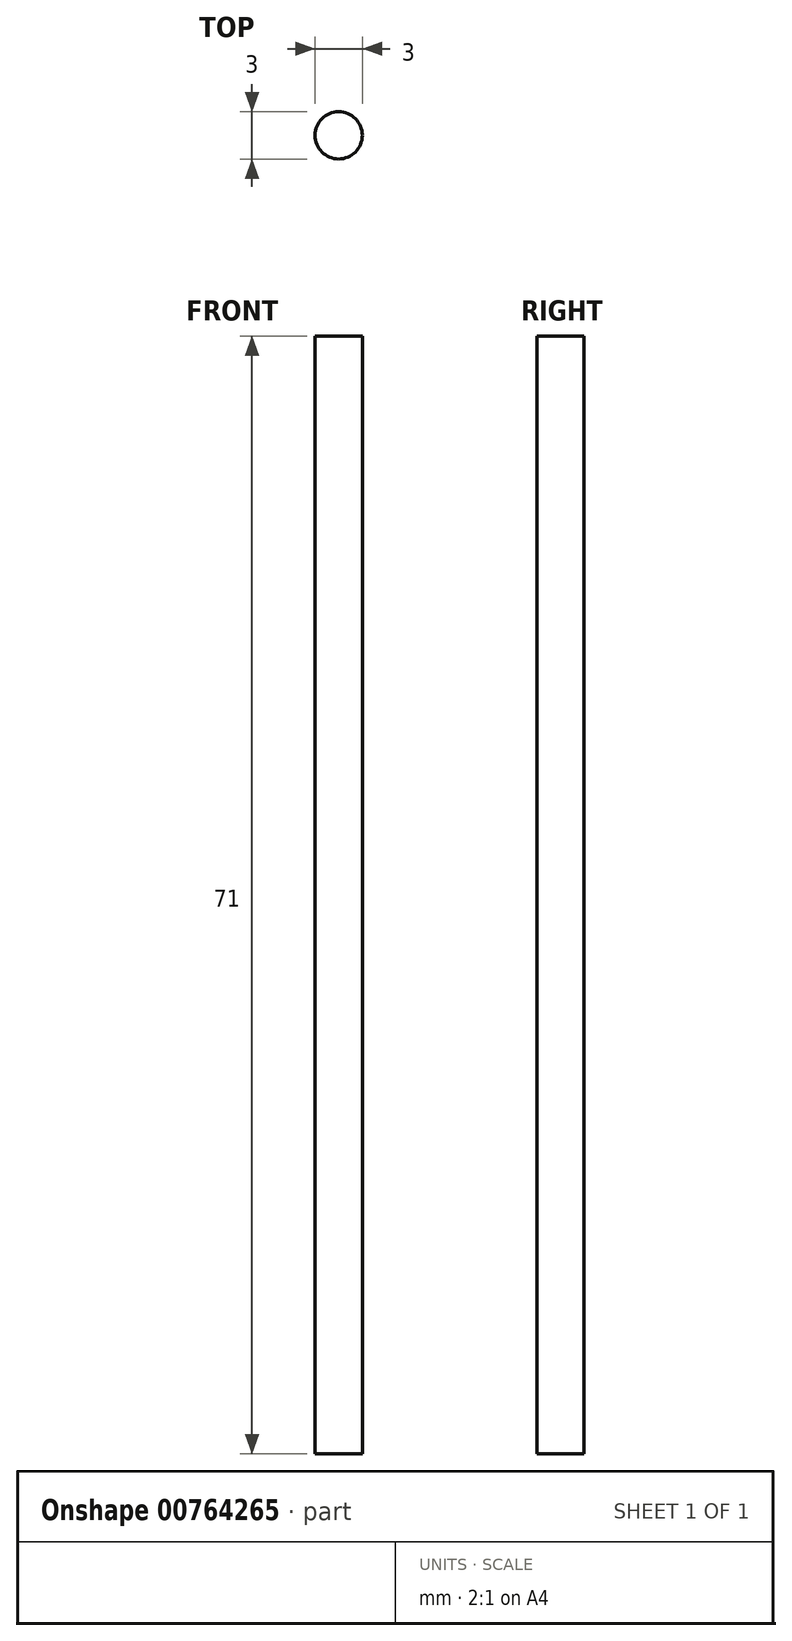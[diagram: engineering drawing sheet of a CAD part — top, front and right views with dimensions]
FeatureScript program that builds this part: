
annotation { "Feature Type Name" : "Feature", "Feature Type Description" : "" }
export const myFeature = defineFeature(function(context is Context, id is Id, definition is map)
    precondition{}
    {
        {
            var Q0;
            Q0=qCreatedBy(makeId("Top.planeOp"),FACE);
            var sketch = newSketch(context, id + "F0", { "sketchPlane" : qUnion([Q0])});
            skCircle(sketch, "E0", {"center": v(0, 0) * mm, "radius": 1.5 * mm});
            skSolve(sketch);
        }
        {
            var Q0;
            Q0 = qSketchRegion(id + "F0", true);
            extrude(context, id + "F1", {"entities" : qUnion([Q0]), "depth" : 71 * mm, "offsetDistance" : 25 * mm});
        }
    });
